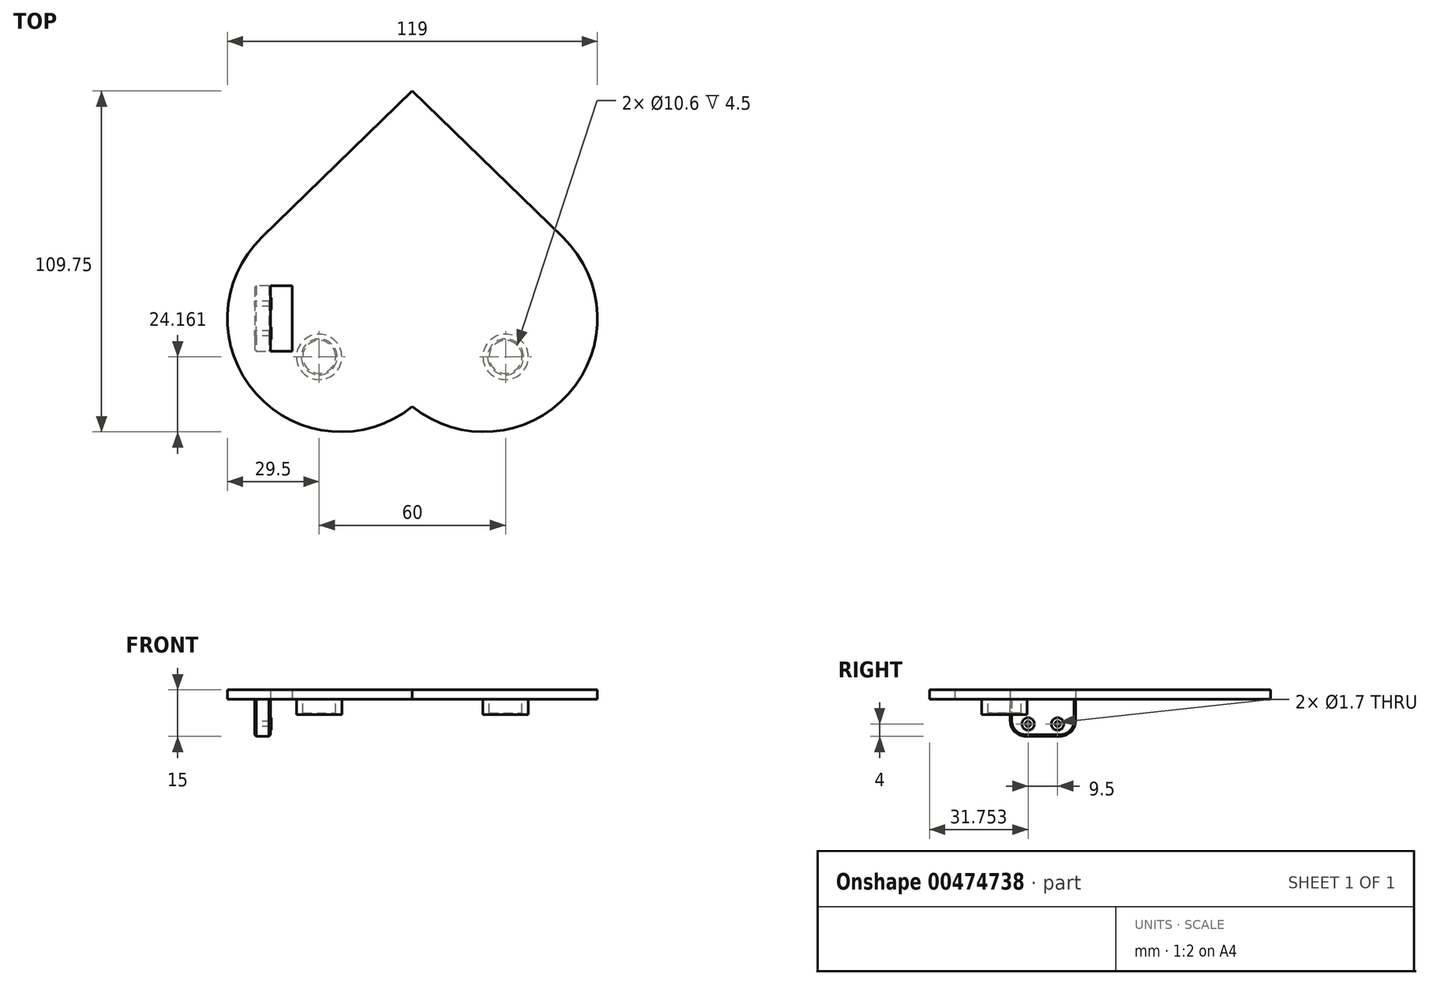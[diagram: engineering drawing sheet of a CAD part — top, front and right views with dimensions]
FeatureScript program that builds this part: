
annotation { "Feature Type Name" : "Feature", "Feature Type Description" : "" }
export const myFeature = defineFeature(function(context is Context, id is Id, definition is map)
    precondition{}
    {
        {
            var Q0;
            Q0=qCreatedBy(makeId("Top.planeOp"),FACE);
            var sketch = newSketch(context, id + "F0", { "sketchPlane" : qUnion([Q0])});
            skLineSegment(sketch, "E0", {"start": v(0, 102.93) * mm, "end": v(-48.79, 55.52) * mm, "construction": true});
            skArc(sketch, "E1", {"start": v(-48.79, 55.52) * mm, "mid": v(-50.8, 4.56) * mm, "end": v(0, 0) * mm, "construction": true});
            skArc(sketch, "E2", {"start": v(0, 0) * mm, "mid": v(50.8, 4.56) * mm, "end": v(48.79, 55.52) * mm, "construction": true});
            skLineSegment(sketch, "E3", {"start": v(0, 102.93) * mm, "end": v(48.79, 55.52) * mm, "construction": true});
            skLineSegment(sketch, "E4", {"start": v(0, 102.93) * mm, "end": v(0, 0) * mm, "construction": true});
            skLineSegment(sketch, "E5", {"start": v(-23, 28.98) * mm, "end": v(23, 28.98) * mm, "construction": true});
            skLineSegment(sketch, "E6", {"start": v(0, 102.23) * mm, "end": v(-48.44, 55.16) * mm});
            skArc(sketch, "E7", {"start": v(-48.44, 55.16) * mm, "mid": v(-50.29, 4.74) * mm, "end": v(0, 0.64) * mm});
            skArc(sketch, "E8", {"start": v(0, 0.64) * mm, "mid": v(50.29, 4.74) * mm, "end": v(48.44, 55.16) * mm});
            skLineSegment(sketch, "E9", {"start": v(0, 102.23) * mm, "end": v(48.44, 55.16) * mm});
            skSolve(sketch);
        }
        {
            var Q0;
            Q0 = qSketchRegion(id + "F0", true);
            extrude(context, id + "F1", {"entities" : qUnion([Q0]), "depth" : 3 * mm, "offsetDistance" : 25 * mm});
        }
        {
            var Q0;
            Q0=makeQuery(id+"F1.opExtrude","CAP_FACE",FACE,{"disambiguationData":[OSD([sQuery(id+"F0.wireOp",EDGE,"E6"),sQuery(id+"F0.wireOp",EDGE,"E7"),sQuery(id+"F0.wireOp",EDGE,"E8"),sQuery(id+"F0.wireOp",EDGE,"E9")])],"isStart":true});
            var sketch = newSketch(context, id + "F2", { "sketchPlane" : qUnion([Q0])});
            skArc(sketch, "E10", {"start": v(0, -14.84) * mm, "mid": v(-39.88, -7.91) * mm, "end": v(-41.82, -48.35) * mm, "construction": true});
            skArc(sketch, "E11", {"start": v(41.82, -48.35) * mm, "mid": v(39.88, -7.91) * mm, "end": v(0, -14.84) * mm, "construction": true});
            skLineSegment(sketch, "E12", {"start": v(-41.82, -48.35) * mm, "end": v(0, -88.98) * mm, "construction": true});
            skLineSegment(sketch, "E13", {"start": v(0, -88.98) * mm, "end": v(41.82, -48.35) * mm, "construction": true});
            skLineSegment(sketch, "E14.bottom", {"start": v(-45.69, -18.48) * mm, "end": v(-38.69, -18.48) * mm});
            skLineSegment(sketch, "E14.top", {"start": v(-45.69, -39.48) * mm, "end": v(-38.69, -39.48) * mm});
            skLineSegment(sketch, "E14.left", {"start": v(-45.69, -18.48) * mm, "end": v(-45.69, -39.48) * mm});
            skLineSegment(sketch, "E14.right", {"start": v(-38.69, -18.48) * mm, "end": v(-38.69, -39.48) * mm});
            skSolve(sketch);
        }
        {
            var Q0;
            Q0 = qSketchRegion(id + "F2", true);
            extrude(context, id + "F3", {"entities" : qUnion([Q0]), "operationType" : NewBodyOperationType.REMOVE, "endBound" : BoundingType.THROUGH_ALL, "oppositeDirection" : true, "depth" : 25 * mm, "offsetDistance" : 25 * mm});
        }
        {
            var Q0;
            Q0=makeQuery(id+"F1.opExtrude","CAP_FACE",FACE,{"disambiguationData":[OSD([sQuery(id+"F0.wireOp",EDGE,"E6"),sQuery(id+"F0.wireOp",EDGE,"E7"),sQuery(id+"F0.wireOp",EDGE,"E8"),sQuery(id+"F0.wireOp",EDGE,"E9")])],"isStart":true});
            var sketch = newSketch(context, id + "F4", { "sketchPlane" : qUnion([Q0])});
            skLineSegment(sketch, "E15", {"start": v(-45.69, -18.48) * mm, "end": v(-45.69, -39.48) * mm});
            skLineSegment(sketch, "E16", {"start": v(-45.69, -39.48) * mm, "end": v(-50.69, -39.48) * mm});
            skLineSegment(sketch, "E17", {"start": v(-50.69, -39.48) * mm, "end": v(-50.69, -18.48) * mm});
            skLineSegment(sketch, "E18", {"start": v(-50.69, -18.48) * mm, "end": v(-45.69, -18.48) * mm});
            skSolve(sketch);
        }
        {
            var Q0;
            Q0 = qSketchRegion(id + "F4", true);
            extrude(context, id + "F5", {"entities" : qUnion([Q0]), "operationType" : NewBodyOperationType.ADD, "depth" : 12 * mm, "offsetDistance" : 25 * mm});
        }
        {
            var Q0;
            Q0=makeQuery(id+"F5.opExtrude","SWEPT_FACE",FACE,{"disambiguationData":[OSD([sQuery(id+"F4.wireOp",EDGE,"E17")])]});
            var sketch = newSketch(context, id + "F6", { "sketchPlane" : qUnion([Q0])});
            skLineSegment(sketch, "E19", {"start": v(-33.73, -8) * mm, "end": v(-24.23, -8) * mm, "construction": true});
            skCircle(sketch, "E20", {"center": v(-33.73, -8) * mm, "radius": 0.85 * mm});
            skCircle(sketch, "E21", {"center": v(-24.23, -8) * mm, "radius": 0.85 * mm});
            skLineSegment(sketch, "E22", {"start": v(-28.98, 0) * mm, "end": v(-28.98, -12) * mm, "construction": true});
            skSolve(sketch);
        }
        {
            var Q0;
            Q0 = qSketchRegion(id + "F6", true);
            extrude(context, id + "F7", {"entities" : qUnion([Q0]), "operationType" : NewBodyOperationType.REMOVE, "endBound" : BoundingType.UP_TO_NEXT, "oppositeDirection" : true, "depth" : 25 * mm, "offsetDistance" : 25 * mm});
        }
        {
            var Q0;
            Q0=makeQuery(id+"F5.opExtrude","CAP_EDGE",EDGE,{"disambiguationData":[OSD([sQuery(id+"F4.wireOp",EDGE,"E16")])],"isStart":false});
            var Q1;
            Q1=makeQuery(id+"F5.opExtrude","CAP_EDGE",EDGE,{"disambiguationData":[OSD([sQuery(id+"F4.wireOp",EDGE,"E18")])],"isStart":false});
            fillet(context, id + "F8", {"entities" : qUnion([Q0, Q1]), "radius" : 5 * mm, "tangentPropagation" : true, "allowEdgeOverflow" : false});
        }
        {
            var Q0;
            Q0=makeQuery(id+"F5.opExtrude","CAP_EDGE",EDGE,{"disambiguationData":[OSD([sQuery(id+"F4.wireOp",EDGE,"E17")])],"isStart":false});
            var Q1;
            Q1=makeQuery(id+"F5.opExtrude","CAP_EDGE",EDGE,{"disambiguationData":[OSD([sQuery(id+"F4.wireOp",EDGE,"E15")])],"isStart":false});
            chamfer(context, id + "F9", {"entities" : qUnion([Q0, Q1]), "width" : 0.5 * mm, "tangentPropagation" : true});
        }
        {
            var Q0;
            Q0=makeQuery(id+"F5.boolean.opBoolean","MERGE",FACE,{"derivedFrom":[makeQuery(id+"F3.boolean.opBoolean","COPY",FACE,{"derivedFrom":makeQuery(id+"F3.opExtrude","SWEPT_FACE",FACE,{"disambiguationData":[OSD([sQuery(id+"F2.wireOp",EDGE,"E14.left")])]})}),makeQuery(id+"F5.opExtrude","SWEPT_FACE",FACE,{"disambiguationData":[OSD([sQuery(id+"F4.wireOp",EDGE,"E15")])]})]});
            var sketch = newSketch(context, id + "F10", { "sketchPlane" : qUnion([Q0])});
            skCircle(sketch, "E23", {"center": v(24.23, -8) * mm, "radius": 2 * mm});
            skCircle(sketch, "E24", {"center": v(33.73, -8) * mm, "radius": 2 * mm});
            skCircle(sketch, "E25", {"center": v(24.23, -8) * mm, "radius": 0.85 * mm});
            skCircle(sketch, "E26", {"center": v(33.73, -8) * mm, "radius": 0.85 * mm});
            skSolve(sketch);
        }
        {
            var Q0;
            Q0 = qSketchRegion(id + "F10", true);
            extrude(context, id + "F11", {"entities" : qUnion([Q0]), "operationType" : NewBodyOperationType.ADD, "depth" : 0.3 * mm, "offsetDistance" : 25 * mm});
        }
        {
            var Q0;
            Q0=makeQuery(id+"F1.opExtrude","CAP_FACE",FACE,{"disambiguationData":[OSD([sQuery(id+"F0.wireOp",EDGE,"E6"),sQuery(id+"F0.wireOp",EDGE,"E7"),sQuery(id+"F0.wireOp",EDGE,"E8"),sQuery(id+"F0.wireOp",EDGE,"E9")])],"isStart":true});
            var sketch = newSketch(context, id + "F12", { "sketchPlane" : qUnion([Q0])});
            skCircle(sketch, "E27", {"center": v(-30, -16.64) * mm, "radius": 7.3 * mm});
            skCircle(sketch, "E28", {"center": v(-30, -16.64) * mm, "radius": 5.3 * mm});
            skCircle(sketch, "E29", {"center": v(30, -16.64) * mm, "radius": 7.3 * mm});
            skCircle(sketch, "E30", {"center": v(30, -16.64) * mm, "radius": 5.3 * mm});
            skLineSegment(sketch, "E31", {"start": v(0, -0.64) * mm, "end": v(0, -102.23) * mm, "construction": true});
            skLineSegment(sketch, "E32", {"start": v(-30, -16.64) * mm, "end": v(30, -16.64) * mm, "construction": true});
            skSolve(sketch);
        }
        {
            var Q0;
            Q0 = qSketchRegion(id + "F12", true);
            extrude(context, id + "F13", {"entities" : qUnion([Q0]), "operationType" : NewBodyOperationType.ADD, "depth" : 5 * mm, "offsetDistance" : 25 * mm});
        }
        {
            var Q0;
            Q0=makeQuery(id+"F13.opExtrude","CAP_EDGE",EDGE,{"disambiguationData":[OSD([sQuery(id+"F12.wireOp",EDGE,"E28")])],"isStart":false});
            var Q1;
            Q1=makeQuery(id+"F13.opExtrude","CAP_EDGE",EDGE,{"disambiguationData":[OSD([sQuery(id+"F12.wireOp",EDGE,"E30")])],"isStart":false});
            chamfer(context, id + "F14", {"entities" : qUnion([Q0, Q1]), "width" : 0.5 * mm, "tangentPropagation" : true});
        }
    });
